# Revit family: NTO_MorseTableSection_NOMSAU90
name_source: partatom
category: Furniture
units: mm (PartAtom-declared; Revit-internal decimal feet)

## family parameters
Always vertical = Yes
Cut with Voids When Loaded = No
Room Calculation Point = No
Shared = Yes
Work Plane-Based = No

## types (4) — shared parameters
AssetType = Moveable
BIMObjectName = NTO_MorseTableSection_NOMSAU90
Category = Pr_40_50_21 : Desks and tables
Color = Black legs, RAL 9005. Black underframe, RAL 9005. White MFMDF top with matching edge.
DurationUnit = Year
ExpectedLife = 10
Features = Legs available in 16 RALs + Oak. Underframe available in 16 RALs. Table top available in White or black MFMDF,  or Forbo Desktop Lino (except for Burgundy) with matching edge colour.
Finish = Steel leg and underframe. MFMDF top.
IfcExportAs = IfcFurnitureType
Leg Hardware Material = NTO_FinishBlack_RAL9005
Leg Material = NTO_Finish_Oak
MainColor = Black legs, RAL 9005. Black underframe, RAL 9005. White MFMDF top with matching edge.
Manufacturer = NaughtOne
ManufacturerName = NaughtOne
ManufacturerURL = www.naughtone.com
Material = Legs in steel or solid oak. Underframe in steel. Top in MFMDF, or Forbo Lino bonded to MDF. Colour matched edge.
Model = Morse Table Section Curve 90 deg A - 800D, Radius corner
NBSDescription = Table
NBSReference = 45-35-72/352
NOMSAU903SQ = No
Name = Morse Table Section Curve 90 deg A - 800D, Radius corner
NominalLength = 1000 mm  [stored 3.28084 ft]
NominalWidth = 1000 mm  [stored 3.28084 ft]
Shape = Rectangular
TableTopMaterial = NTO_Finish_TableTopWhite
URL = www.naughtone.com
Uniclass2015Code = Pr_40_50_21
Uniclass2015Title = Desks and tables
Uniclass2015Version = Products v1.30
Version = 1
WarrantyDescription = 10 Years
WarrantyDurationUnit = Year
zero-valued in all types: Default Elevation

## per-type parameters (varying)
| type | CircularEnd | Description | IfcExportType | Keynote | LegHeight | ModelReference | NominalHeight | ProductInformation | Size | SquareEnd |
| NOMSAU905RD | Yes | Morse Bar Height Table Section Curve 90 deg A - 800D, Radius corner | Chair | NOPIP10GLN
NOPIP10GLN | 1025 mm  [stored 3.36286 ft] | Morse Bar Height Table Section Curve 90 deg A - 800D, Radius corner | 1050 mm | www.naughtone.com/products/pippin | 1000 x 1000 x 1050 mm
530 x 760 x 760 mm | No |
| NOMSAU905SQ | No | Morse Bar Height Table Section Curve 90 deg A - 800D, Square corner |  | NOMSAU905SQ | 1025 mm  [stored 3.36286 ft] | Morse Bar Height Table Section Curve 90 deg A - 800D, Square corner | 1050 mm | www.naughtone.com/products/morse | 1000 x 1000 x 1050 mm | Yes |
| NOMSAU903RD | Yes | Morse Table Section Curve 90 deg A - 800D, Radius corner | Chair | NOMSAU903RD | 705 mm  [stored 2.31299 ft] | Morse Table Section Curve 90 deg A - 800D, Radius corner | 730 mm  [stored 2.39501 ft] | www.naughtone.com/products/pippin | 1000 x 1000 x 730 mm
530 x 760 x 760 mm | No |
| NOMSAU903SQ | No | Morse Table Section Curve 90 deg A - 800D, Square corner | Chair | NOPIP10GLN
NOPIP10GLN | 705 mm  [stored 2.31299 ft] | Morse Table Section Curve 90 deg A - 800D, Square corner | 730 mm  [stored 2.39501 ft] | www.naughtone.com/products/pippin | 1000 x 1000 x 730 mm
530 x 760 x 760 mm | Yes |

note: column(s) folded — value = type name in every type: ModelNumber

note: [stored X ft] marks values corroborated as IEEE doubles in the binary element streams (Revit-internal decimal feet)

## geometry (parser evidence)
native form markers: Sweep x15
no freeform markers — native parametric forms only
